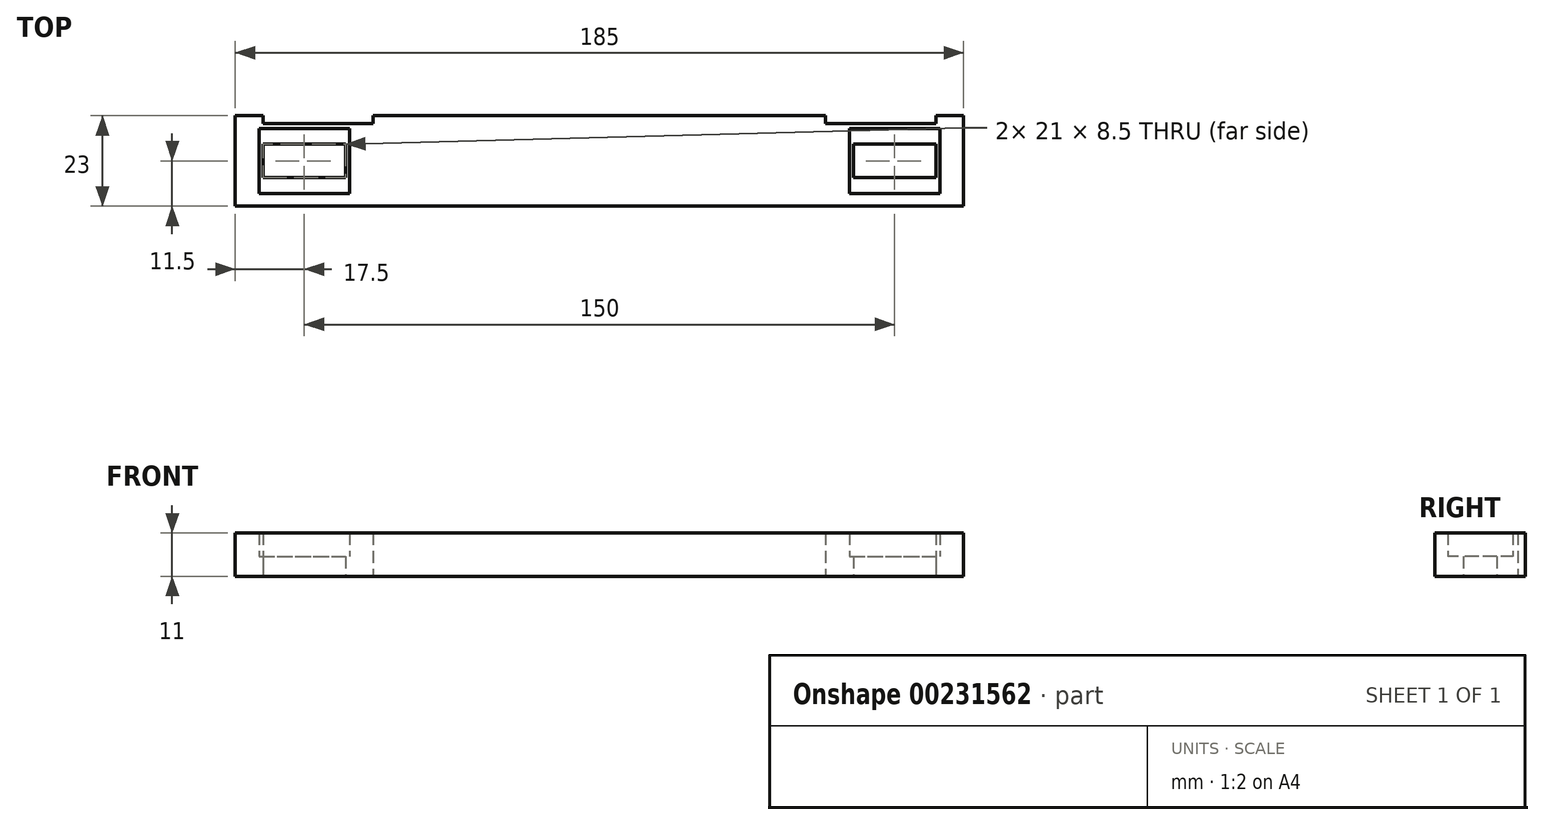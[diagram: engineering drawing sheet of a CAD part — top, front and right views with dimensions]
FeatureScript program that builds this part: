
annotation { "Feature Type Name" : "Feature", "Feature Type Description" : "" }
export const myFeature = defineFeature(function(context is Context, id is Id, definition is map)
    precondition{}
    {
        {
            var Q0;
            Q0=qCreatedBy(makeId("Top.planeOp"),FACE);
            var sketch = newSketch(context, id + "F0", { "sketchPlane" : qUnion([Q0])});
            skLineSegment(sketch, "E0.bottom", {"start": v(-92.5, 11.5) * mm, "end": v(92.5, 11.5) * mm});
            skLineSegment(sketch, "E0.top", {"start": v(-92.5, -11.5) * mm, "end": v(92.5, -11.5) * mm});
            skLineSegment(sketch, "E0.left", {"start": v(-92.5, 11.5) * mm, "end": v(-92.5, -11.5) * mm});
            skLineSegment(sketch, "E0.right", {"start": v(92.5, 11.5) * mm, "end": v(92.5, -11.5) * mm});
            skLineSegment(sketch, "E1.bottom", {"start": v(64.5, 4.25) * mm, "end": v(85.5, 4.25) * mm});
            skLineSegment(sketch, "E1.top", {"start": v(64.5, -4.25) * mm, "end": v(85.5, -4.25) * mm});
            skLineSegment(sketch, "E1.left", {"start": v(64.5, 4.25) * mm, "end": v(64.5, -4.25) * mm});
            skLineSegment(sketch, "E1.right", {"start": v(85.5, 4.25) * mm, "end": v(85.5, -4.25) * mm});
            skLineSegment(sketch, "E2.bottom", {"start": v(63.5, 8.25) * mm, "end": v(86.5, 8.25) * mm});
            skLineSegment(sketch, "E2.top", {"start": v(63.5, -8.25) * mm, "end": v(86.5, -8.25) * mm});
            skLineSegment(sketch, "E2.left", {"start": v(63.5, 8.25) * mm, "end": v(63.5, -8.25) * mm});
            skLineSegment(sketch, "E2.right", {"start": v(86.5, 8.25) * mm, "end": v(86.5, -8.25) * mm});
            skLineSegment(sketch, "E3.bottom", {"start": v(-86.5, 8.25) * mm, "end": v(-63.5, 8.25) * mm});
            skLineSegment(sketch, "E3.top", {"start": v(-86.5, -8.25) * mm, "end": v(-63.5, -8.25) * mm});
            skLineSegment(sketch, "E3.left", {"start": v(-86.5, 8.25) * mm, "end": v(-86.5, -8.25) * mm});
            skLineSegment(sketch, "E3.right", {"start": v(-63.5, 8.25) * mm, "end": v(-63.5, -8.25) * mm});
            skLineSegment(sketch, "E4.bottom", {"start": v(-85.5, 4.25) * mm, "end": v(-64.5, 4.25) * mm});
            skLineSegment(sketch, "E4.top", {"start": v(-85.5, -4.25) * mm, "end": v(-64.5, -4.25) * mm});
            skLineSegment(sketch, "E4.left", {"start": v(-85.5, 4.25) * mm, "end": v(-85.5, -4.25) * mm});
            skLineSegment(sketch, "E4.right", {"start": v(-64.5, 4.25) * mm, "end": v(-64.5, -4.25) * mm});
            skLineSegment(sketch, "E5.bottom", {"start": v(57.5, 11.5) * mm, "end": v(85.5, 11.5) * mm});
            skLineSegment(sketch, "E5.top", {"start": v(57.5, 9.5) * mm, "end": v(85.5, 9.5) * mm});
            skLineSegment(sketch, "E5.left", {"start": v(57.5, 11.5) * mm, "end": v(57.5, 9.5) * mm});
            skLineSegment(sketch, "E5.right", {"start": v(85.5, 11.5) * mm, "end": v(85.5, 9.5) * mm});
            skLineSegment(sketch, "E6.bottom", {"start": v(-85.5, 11.5) * mm, "end": v(-57.5, 11.5) * mm});
            skLineSegment(sketch, "E6.top", {"start": v(-85.5, 9.5) * mm, "end": v(-57.5, 9.5) * mm});
            skLineSegment(sketch, "E6.left", {"start": v(-85.5, 11.5) * mm, "end": v(-85.5, 9.5) * mm});
            skLineSegment(sketch, "E6.right", {"start": v(-57.5, 11.5) * mm, "end": v(-57.5, 9.5) * mm});
            skSolve(sketch);
        }
        {
            var Q0;
            Q0=makeQuery(id+"F0.imprint","IMPRINT",FACE,{"disambiguationData":[TD([[makeQuery(id+"F0.imprint","IMPRINT",EDGE,{"derivedFrom":sQuery(id+"F0.wireOp",EDGE,"E0.top")}),1.0]])]});
            extrude(context, id + "F1", {"entities" : qUnion([Q0]), "depth" : 11 * mm});
        }
        {
            var Q0;
            Q0=makeQuery(id+"F0.imprint","IMPRINT",FACE,{"disambiguationData":[TD([[makeQuery(id+"F0.imprint","IMPRINT",EDGE,{"derivedFrom":sQuery(id+"F0.wireOp",EDGE,"E0.top")}),1.0]])]});
            var Q1;
            Q1=makeQuery(id+"F0.imprint","IMPRINT",FACE,{"disambiguationData":[TD([[makeQuery(id+"F0.imprint","IMPRINT",EDGE,{"derivedFrom":sQuery(id+"F0.wireOp",EDGE,"E1.bottom")}),1.0]])]});
            var Q2;
            Q2=makeQuery(id+"F0.imprint","IMPRINT",FACE,{"disambiguationData":[TD([[makeQuery(id+"F0.imprint","IMPRINT",EDGE,{"derivedFrom":sQuery(id+"F0.wireOp",EDGE,"E3.bottom")}),-1.0]])]});
            extrude(context, id + "F2", {"entities" : qUnion([Q0, Q1, Q2]), "operationType" : NewBodyOperationType.ADD, "depth" : 5 * mm});
        }
    });
